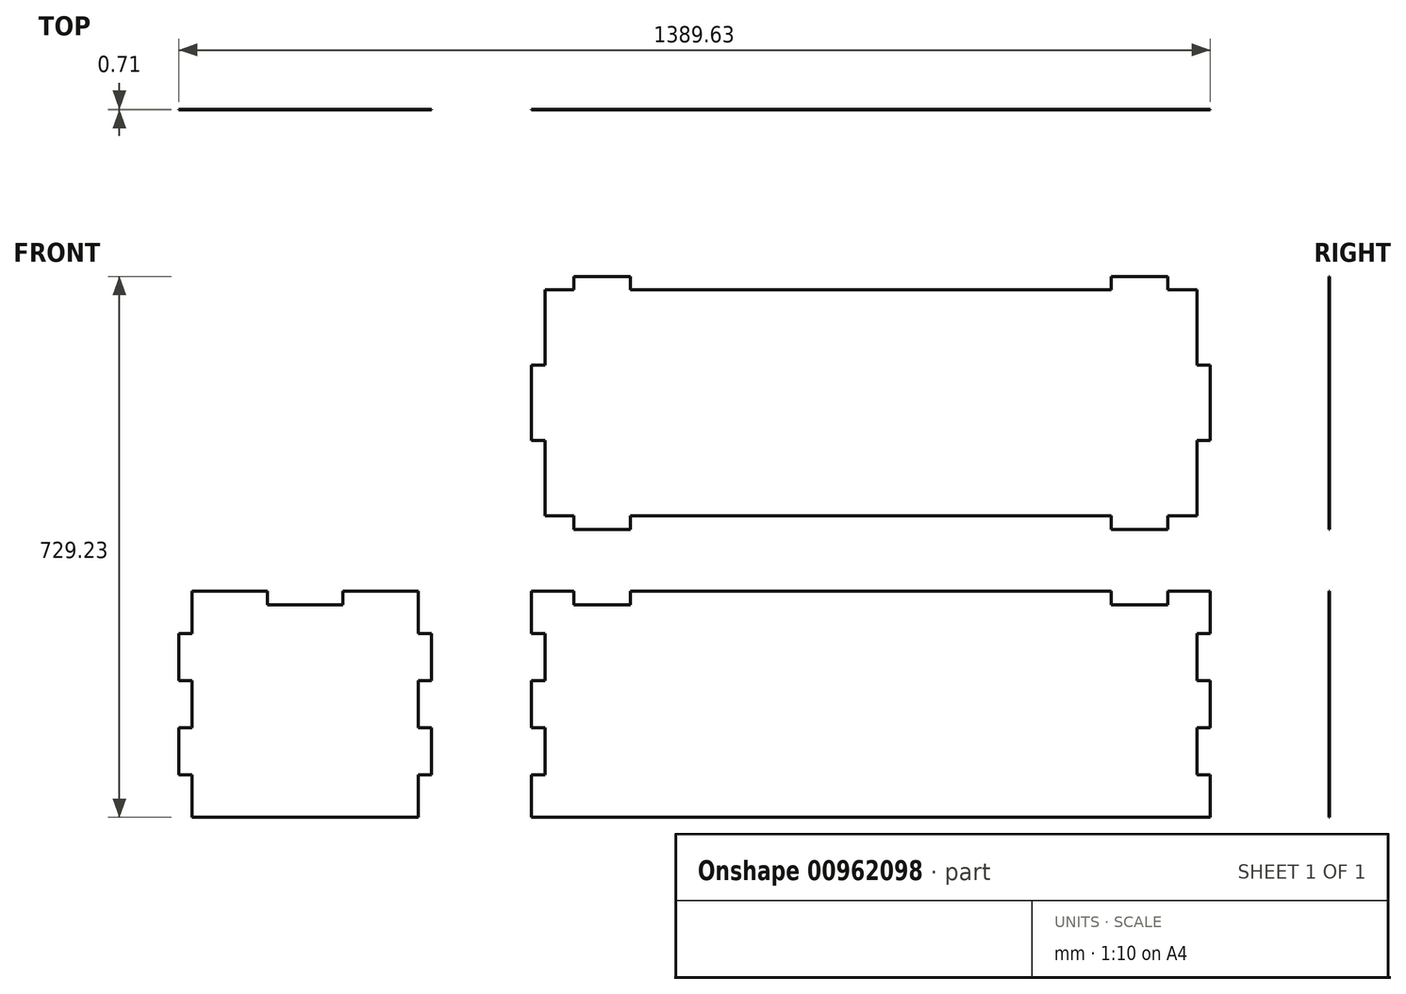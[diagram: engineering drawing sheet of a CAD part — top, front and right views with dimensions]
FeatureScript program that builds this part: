
annotation { "Feature Type Name" : "Feature", "Feature Type Description" : "" }
export const myFeature = defineFeature(function(context is Context, id is Id, definition is map)
    precondition{}
    {
        {
            assignVariable(context, id + "F0", {"name" : "ply34", "anyValue" : .71});
        }
        {
            var Q0;
            Q0=qCreatedBy(makeId("Front.planeOp"),FACE);
            var sketch = newSketch(context, id + "F1", { "sketchPlane" : qUnion([Q0])});
            skLineSegment(sketch, "E0.bottom", {"start": v(-457.2, 152.4) * mm, "end": v(457.2, 152.4) * mm});
            skLineSegment(sketch, "E0.top", {"start": v(-457.2, -152.4) * mm, "end": v(457.2, -152.4) * mm});
            skLineSegment(sketch, "E0.left", {"start": v(-457.2, 152.4) * mm, "end": v(-457.2, -152.4) * mm});
            skLineSegment(sketch, "E0.right", {"start": v(457.2, 152.4) * mm, "end": v(457.2, -152.4) * mm});
            skPoint(sketch, "E0.middle", {"position": v(0, 0) * mm});
            skLineSegment(sketch, "E1.bottom", {"start": v(-609.6, 152.4) * mm, "end": v(-914.4, 152.4) * mm});
            skLineSegment(sketch, "E1.top", {"start": v(-609.6, -152.4) * mm, "end": v(-914.4, -152.4) * mm});
            skLineSegment(sketch, "E1.left", {"start": v(-609.6, 152.4) * mm, "end": v(-609.6, -152.4) * mm});
            skLineSegment(sketch, "E1.right", {"start": v(-914.4, 152.4) * mm, "end": v(-914.4, -152.4) * mm});
            skLineSegment(sketch, "E2.bottom", {"start": v(-609.6, 95.25) * mm, "end": v(-591.57, 95.25) * mm});
            skLineSegment(sketch, "E2.top", {"start": v(-609.6, 31.75) * mm, "end": v(-591.57, 31.75) * mm});
            skLineSegment(sketch, "E2.left", {"start": v(-609.6, 95.25) * mm, "end": v(-609.6, 31.75) * mm});
            skLineSegment(sketch, "E2.right", {"start": v(-591.57, 95.25) * mm, "end": v(-591.57, 31.75) * mm});
            skLineSegment(sketch, "E3", {"start": v(-457.2, 0) * mm, "end": v(-609.6, 0) * mm, "construction": true});
            skLineSegment(sketch, "E4.MirrorCS", {"start": v(-609.6, -95.25) * mm, "end": v(-591.57, -95.25) * mm});
            skLineSegment(sketch, "E5.MirrorCS", {"start": v(-609.6, -31.75) * mm, "end": v(-591.57, -31.75) * mm});
            skLineSegment(sketch, "E6.MirrorCS", {"start": v(-609.6, -95.25) * mm, "end": v(-609.6, -31.75) * mm});
            skLineSegment(sketch, "E7.MirrorCS", {"start": v(-591.57, -95.25) * mm, "end": v(-591.57, -31.75) * mm});
            skLineSegment(sketch, "E8", {"start": v(-591.57, 63.5) * mm, "end": v(-457.2, 63.5) * mm, "construction": true});
            skLineSegment(sketch, "E9", {"start": v(-524.38, 63.5) * mm, "end": v(-524.38, 0) * mm, "construction": true});
            skLineSegment(sketch, "E10.MirrorCS", {"start": v(-439.17, 95.25) * mm, "end": v(-457.2, 95.25) * mm});
            skLineSegment(sketch, "E11.MirrorCS", {"start": v(-439.17, -95.25) * mm, "end": v(-457.2, -95.25) * mm});
            skLineSegment(sketch, "E12.MirrorCS", {"start": v(-439.17, 31.75) * mm, "end": v(-457.2, 31.75) * mm});
            skLineSegment(sketch, "E13.MirrorCS", {"start": v(-439.17, -31.75) * mm, "end": v(-457.2, -31.75) * mm});
            skLineSegment(sketch, "E14.MirrorCS", {"start": v(-439.17, 95.25) * mm, "end": v(-439.17, 31.75) * mm});
            skLineSegment(sketch, "E15.MirrorCS", {"start": v(-457.2, -95.25) * mm, "end": v(-457.2, -31.75) * mm});
            skLineSegment(sketch, "E16.MirrorCS", {"start": v(-457.2, 95.25) * mm, "end": v(-457.2, 31.75) * mm});
            skLineSegment(sketch, "E17.MirrorCS", {"start": v(-439.17, -95.25) * mm, "end": v(-439.17, -31.75) * mm});
            skLineSegment(sketch, "E18", {"start": v(-762, 152.4) * mm, "end": v(-762, -152.4) * mm, "construction": true});
            skLineSegment(sketch, "E19", {"start": v(0, 152.4) * mm, "end": v(0, -152.4) * mm, "construction": true});
            skLineSegment(sketch, "E20.MirrorCS", {"start": v(-932.43, 95.25) * mm, "end": v(-932.43, 31.75) * mm});
            skLineSegment(sketch, "E21.MirrorCS", {"start": v(-914.4, 31.75) * mm, "end": v(-932.43, 31.75) * mm});
            skLineSegment(sketch, "E22.MirrorCS", {"start": v(-914.4, -95.25) * mm, "end": v(-932.43, -95.25) * mm});
            skLineSegment(sketch, "E23.MirrorCS", {"start": v(-914.4, -31.75) * mm, "end": v(-932.43, -31.75) * mm});
            skLineSegment(sketch, "E24.MirrorCS", {"start": v(-914.4, 95.25) * mm, "end": v(-932.43, 95.25) * mm});
            skLineSegment(sketch, "E25.MirrorCS", {"start": v(-914.4, 95.25) * mm, "end": v(-914.4, 31.75) * mm});
            skLineSegment(sketch, "E26.MirrorCS", {"start": v(-932.43, -95.25) * mm, "end": v(-932.43, -31.75) * mm});
            skLineSegment(sketch, "E27.MirrorCS", {"start": v(-914.4, -95.25) * mm, "end": v(-914.4, -31.75) * mm});
            skLineSegment(sketch, "E28.MirrorCS", {"start": v(439.17, -31.75) * mm, "end": v(457.2, -31.75) * mm});
            skLineSegment(sketch, "E29.MirrorCS", {"start": v(439.17, -95.25) * mm, "end": v(457.2, -95.25) * mm});
            skLineSegment(sketch, "E30.MirrorCS", {"start": v(439.17, 31.75) * mm, "end": v(457.2, 31.75) * mm});
            skLineSegment(sketch, "E31.MirrorCS", {"start": v(439.17, 95.25) * mm, "end": v(457.2, 95.25) * mm});
            skLineSegment(sketch, "E32.MirrorCS", {"start": v(457.2, 95.25) * mm, "end": v(457.2, 31.75) * mm});
            skLineSegment(sketch, "E33.MirrorCS", {"start": v(457.2, -95.25) * mm, "end": v(457.2, -31.75) * mm});
            skLineSegment(sketch, "E34.MirrorCS", {"start": v(439.17, -95.25) * mm, "end": v(439.17, -31.75) * mm});
            skLineSegment(sketch, "E35.MirrorCS", {"start": v(439.17, 95.25) * mm, "end": v(439.17, 31.75) * mm});
            skLineSegment(sketch, "E36.bottom", {"start": v(-400.05, 152.4) * mm, "end": v(-323.85, 152.4) * mm});
            skLineSegment(sketch, "E36.top", {"start": v(-400.05, 134.37) * mm, "end": v(-323.85, 134.37) * mm});
            skLineSegment(sketch, "E36.left", {"start": v(-400.05, 152.4) * mm, "end": v(-400.05, 134.37) * mm});
            skLineSegment(sketch, "E36.right", {"start": v(-323.85, 152.4) * mm, "end": v(-323.85, 134.37) * mm});
            skLineSegment(sketch, "E37.MirrorCS", {"start": v(400.05, 152.4) * mm, "end": v(400.05, 134.37) * mm});
            skLineSegment(sketch, "E38.MirrorCS", {"start": v(400.05, 152.4) * mm, "end": v(323.85, 152.4) * mm});
            skLineSegment(sketch, "E39.MirrorCS", {"start": v(400.05, 134.37) * mm, "end": v(323.85, 134.37) * mm});
            skLineSegment(sketch, "E40.MirrorCS", {"start": v(323.85, 152.4) * mm, "end": v(323.85, 134.37) * mm});
            skLineSegment(sketch, "E41.bottom", {"start": v(-400.05, 254) * mm, "end": v(-323.85, 254) * mm});
            skLineSegment(sketch, "E41.top", {"start": v(-400.05, 235.97) * mm, "end": v(-323.85, 235.97) * mm});
            skLineSegment(sketch, "E41.left", {"start": v(-400.05, 254) * mm, "end": v(-400.05, 235.97) * mm});
            skLineSegment(sketch, "E41.right", {"start": v(-323.85, 254) * mm, "end": v(-323.85, 235.97) * mm});
            skLineSegment(sketch, "E42.MirrorCS", {"start": v(323.85, 254) * mm, "end": v(323.85, 235.97) * mm});
            skLineSegment(sketch, "E43.MirrorCS", {"start": v(400.05, 235.97) * mm, "end": v(323.85, 235.97) * mm});
            skLineSegment(sketch, "E44.MirrorCS", {"start": v(400.05, 254) * mm, "end": v(323.85, 254) * mm});
            skLineSegment(sketch, "E45.MirrorCS", {"start": v(400.05, 254) * mm, "end": v(400.05, 235.97) * mm});
            skLineSegment(sketch, "E46", {"start": v(-439.17, 406.4) * mm, "end": v(439.17, 406.4) * mm, "construction": true});
            skLineSegment(sketch, "E47.MirrorCS", {"start": v(-323.85, 558.8) * mm, "end": v(-323.85, 576.83) * mm});
            skLineSegment(sketch, "E48.MirrorCS", {"start": v(323.85, 558.8) * mm, "end": v(323.85, 576.83) * mm});
            skLineSegment(sketch, "E49.MirrorCS", {"start": v(400.05, 558.8) * mm, "end": v(323.85, 558.8) * mm});
            skLineSegment(sketch, "E50.MirrorCS", {"start": v(-400.05, 576.83) * mm, "end": v(-323.85, 576.83) * mm});
            skLineSegment(sketch, "E51.MirrorCS", {"start": v(-400.05, 558.8) * mm, "end": v(-323.85, 558.8) * mm});
            skLineSegment(sketch, "E52.MirrorCS", {"start": v(400.05, 558.8) * mm, "end": v(400.05, 576.83) * mm});
            skLineSegment(sketch, "E53.MirrorCS", {"start": v(400.05, 576.83) * mm, "end": v(323.85, 576.83) * mm});
            skLineSegment(sketch, "E54.MirrorCS", {"start": v(-400.05, 558.8) * mm, "end": v(-400.05, 576.83) * mm});
            skLineSegment(sketch, "E55.bottom", {"start": v(-439.17, 254) * mm, "end": v(439.17, 254) * mm});
            skLineSegment(sketch, "E55.top", {"start": v(-439.17, 558.8) * mm, "end": v(439.17, 558.8) * mm});
            skLineSegment(sketch, "E55.left", {"start": v(-439.17, 254) * mm, "end": v(-439.17, 558.8) * mm});
            skLineSegment(sketch, "E55.right", {"start": v(439.17, 254) * mm, "end": v(439.17, 558.8) * mm});
            skLineSegment(sketch, "E56.bottom", {"start": v(-439.17, 457.2) * mm, "end": v(-421.13, 457.2) * mm, "construction": true});
            skLineSegment(sketch, "E56.top", {"start": v(-439.17, 355.6) * mm, "end": v(-421.13, 355.6) * mm, "construction": true});
            skLineSegment(sketch, "E56.left", {"start": v(-439.17, 457.2) * mm, "end": v(-439.17, 355.6) * mm});
            skLineSegment(sketch, "E56.right", {"start": v(-421.13, 457.2) * mm, "end": v(-421.13, 355.6) * mm, "construction": true});
            skPoint(sketch, "E56.middle", {"position": v(-430.15, 406.4) * mm});
            skLineSegment(sketch, "E57.MirrorCS", {"start": v(439.17, 355.6) * mm, "end": v(421.13, 355.6) * mm, "construction": true});
            skLineSegment(sketch, "E58.MirrorCS", {"start": v(439.17, 457.2) * mm, "end": v(421.13, 457.2) * mm, "construction": true});
            skLineSegment(sketch, "E59.MirrorCS", {"start": v(439.17, 457.2) * mm, "end": v(439.17, 355.6) * mm});
            skPoint(sketch, "E60.MirrorP", {"position": v(430.15, 406.4) * mm});
            skLineSegment(sketch, "E61.MirrorCS", {"start": v(421.13, 457.2) * mm, "end": v(421.13, 355.6) * mm, "construction": true});
            skLineSegment(sketch, "E62.MirrorCS", {"start": v(-439.17, 355.6) * mm, "end": v(-457.2, 355.6) * mm});
            skLineSegment(sketch, "E63.MirrorCS", {"start": v(-457.2, 457.2) * mm, "end": v(-457.2, 355.6) * mm});
            skLineSegment(sketch, "E64.MirrorCS", {"start": v(-439.17, 457.2) * mm, "end": v(-457.2, 457.2) * mm});
            skLineSegment(sketch, "E65.MirrorCS", {"start": v(439.17, 355.6) * mm, "end": v(457.2, 355.6) * mm});
            skLineSegment(sketch, "E66.MirrorCS", {"start": v(457.2, 457.2) * mm, "end": v(457.2, 355.6) * mm});
            skLineSegment(sketch, "E67.MirrorCS", {"start": v(439.17, 457.2) * mm, "end": v(457.2, 457.2) * mm});
            skLineSegment(sketch, "E68.bottom", {"start": v(-812.8, 152.4) * mm, "end": v(-711.2, 152.4) * mm});
            skLineSegment(sketch, "E68.top", {"start": v(-812.8, 134.37) * mm, "end": v(-711.2, 134.37) * mm});
            skLineSegment(sketch, "E68.left", {"start": v(-812.8, 152.4) * mm, "end": v(-812.8, 134.37) * mm});
            skLineSegment(sketch, "E68.right", {"start": v(-711.2, 152.4) * mm, "end": v(-711.2, 134.37) * mm});
            skPoint(sketch, "E68.middle", {"position": v(-762, 143.38) * mm});
            skSolve(sketch);
        }
        {
            var Q0;
            {var subQ9=sQuery(id+"F1.wireOp",EDGE,"E1.top");Q0=makeQuery(id+"F1.imprint","IMPRINT",FACE,{"disambiguationData":[TD([[makeQuery(id+"F1.imprint","IMPRINT",EDGE,{"derivedFrom":subQ9}),-1.0]])]});}
            var Q1;
            Q1=makeQuery(id+"F1.imprint","IMPRINT",FACE,{"disambiguationData":[TD([[makeQuery(id+"F1.imprint","IMPRINT",EDGE,{"derivedFrom":sQuery(id+"F1.wireOp",EDGE,"E20.MirrorCS")}),1.0]])]});
            var Q2;
            {var subQ0=sQuery(id+"F1.wireOp",EDGE,"E22.MirrorCS");Q2=makeQuery(id+"F1.imprint","IMPRINT",FACE,{"disambiguationData":[TD([[makeQuery(id+"F1.imprint","IMPRINT",EDGE,{"derivedFrom":subQ0}),-1.0]])]});}
            var Q3;
            {var subQ2=sQuery(id+"F1.wireOp",EDGE,"E2.bottom");Q3=makeQuery(id+"F1.imprint","IMPRINT",FACE,{"disambiguationData":[TD([[makeQuery(id+"F1.imprint","IMPRINT",EDGE,{"derivedFrom":subQ2}),-1.0]])]});}
            var Q4;
            {var subQ0=sQuery(id+"F1.wireOp",EDGE,"E4.MirrorCS");Q4=makeQuery(id+"F1.imprint","IMPRINT",FACE,{"disambiguationData":[TD([[makeQuery(id+"F1.imprint","IMPRINT",EDGE,{"derivedFrom":subQ0}),1.0]])]});}
            var Q5;
            {var subQ15=sQuery(id+"F1.wireOp",EDGE,"E0.top");Q5=makeQuery(id+"F1.imprint","IMPRINT",FACE,{"disambiguationData":[TD([[makeQuery(id+"F1.imprint","IMPRINT",EDGE,{"derivedFrom":subQ15}),1.0]])]});}
            var Q6;
            {var subQ18=sQuery(id+"F1.wireOp",EDGE,"E56.bottom");Q6=makeQuery(id+"F1.imprint","IMPRINT",FACE,{"disambiguationData":[TD([[makeQuery(id+"F1.imprint","IMPRINT",EDGE,{"derivedFrom":subQ18}),1.0]])]});}
            var Q7;
            Q7=makeQuery(id+"F1.imprint","IMPRINT",FACE,{"disambiguationData":[TD([[makeQuery(id+"F1.imprint","IMPRINT",EDGE,{"derivedFrom":sQuery(id+"F1.wireOp",EDGE,"E47.MirrorCS")}),1.0]])]});
            var Q8;
            Q8=makeQuery(id+"F1.imprint","IMPRINT",FACE,{"disambiguationData":[TD([[makeQuery(id+"F1.imprint","IMPRINT",EDGE,{"derivedFrom":sQuery(id+"F1.wireOp",EDGE,"E48.MirrorCS")}),-1.0]])]});
            var Q9;
            Q9=makeQuery(id+"F1.imprint","IMPRINT",FACE,{"disambiguationData":[TD([[makeQuery(id+"F1.imprint","IMPRINT",EDGE,{"derivedFrom":sQuery(id+"F1.wireOp",EDGE,"E42.MirrorCS")}),1.0]])]});
            var Q10;
            Q10=makeQuery(id+"F1.imprint","IMPRINT",FACE,{"disambiguationData":[TD([[makeQuery(id+"F1.imprint","IMPRINT",EDGE,{"derivedFrom":sQuery(id+"F1.wireOp",EDGE,"E41.bottom")}),-1.0]])]});
            var Q11;
            {var subQ6=sQuery(id+"F1.wireOp",EDGE,"E41.bottom");Q11=makeQuery(id+"F1.imprint","IMPRINT",FACE,{"disambiguationData":[TD([[makeQuery(id+"F1.imprint","IMPRINT",EDGE,{"derivedFrom":subQ6}),1.0]])]});}
            var Q12;
            {var subQ2=sQuery(id+"F1.wireOp",EDGE,"E62.MirrorCS");Q12=makeQuery(id+"F1.imprint","IMPRINT",FACE,{"disambiguationData":[TD([[makeQuery(id+"F1.imprint","IMPRINT",EDGE,{"derivedFrom":subQ2}),-1.0]])]});}
            var Q13;
            {var subQ0=sQuery(id+"F1.wireOp",EDGE,"E65.MirrorCS");Q13=makeQuery(id+"F1.imprint","IMPRINT",FACE,{"disambiguationData":[TD([[makeQuery(id+"F1.imprint","IMPRINT",EDGE,{"derivedFrom":subQ0}),1.0]])]});}
            extrude(context, id + "F2", {"entities" : qUnion([Q0, Q1, Q2, Q3, Q4, Q5, Q6, Q7, Q8, Q9, Q10, Q11, Q12, Q13]), "depth" : (getVariable(context, 'ply34')) * mm, "offsetDistance" : 25.4 * mm});
        }
    });
